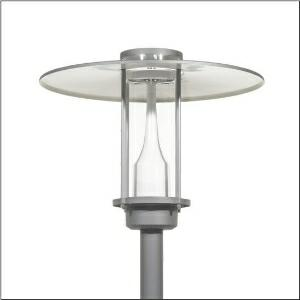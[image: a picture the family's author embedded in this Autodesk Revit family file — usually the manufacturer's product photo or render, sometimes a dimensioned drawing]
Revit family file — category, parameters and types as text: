
# Revit family: city-light_plus_iq___p1_0a_5xa5275ff14hp_3a67
name_source: partatom
category: Lighting Fixtures
units: mm (PartAtom-declared; Revit-internal decimal feet)

## family parameters
Cut with Voids When Loaded = No
Host = Face
Light Source = No
Part Type = Normal
Room Calculation Point = No
Round Connector Dimension = Use Diameter
Shared = No

## types (1)
- --- (1 x LED, 4480 lm, 33.6 W, 3000K)
    Apparent Load = 34 VA
    CIE Flux Codes = 30 60 90 96 100
    Color Rendering = 70
    Color Temperature = 3000K
    Default Elevation = 1800 mm
    Description = City-Light Plus iQ, mast luminaire, Module 540 iQ-SR, primary light control with 3 zone facetted reflector, of plastic, silver coated, highly specular, structured, primary optical cover: cover, of PMMA, transparent, light distribution: P1.0a, light emission: direct distribution, primary light characteristic: strongly asymmetric, installation type: post-top, LED, High Power LED, rated luminous flux: 4.480lm, luminous efficacy: 133lm/W, light colour: 730, colour temperature: 3000K, control gear: iQ Street-Remote, control: pre-setting: logarithmic dimming characteristic, Street-Remote, Auto-Match, Temp-Guard, Lumen-Switch, Night-Set, Smart-Wire, Light-Fading, Desk-Remote (wireless, voltage-free reading and setting of iQ features in the workshop via application-optimized NFC function/RFID function), optimised constant luminous flux control (CLO 2.0), with terminal, 6-pole, max. 2.5mm², mains connection: 230..240V, AC, 50/60Hz, start of lifetime: 34W, end of service life: 36W, reduction: 15W, luminaire housing, upper part, of glass-fibre reinforced polyester, coated, Siteco® metallic grey (DB 702S), diameter: 750mm, height: 590mm, spigot size: d x l = 76 x 70mm (post-top) | with reducer (optional accessory) 60 x 70mm, mounting height: 3..5m, post-top mast mounting element, of diecast aluminium, coated, Siteco® metallic grey (DB 702S), Module 540 iQ-SR, traffic white (RAL 9016), equipment: Power, protection rating (complete): IP65, insulation class (complete): insulation class II (safety insulation), certification: CE, ENEC, VDE, packaging unit: 1 piece

Light Distribution: P1.0a
    Height = 590 mm
    Lamp = 1 x LED
    Lamp Light Flux = 4480 lm
    Lamp Power = 33.6 W
    Lamp count = 1
    Length = 750 mm
    Luminous efficacy = 133 lm/W
    Manufacturer = Siteco
    ModVariant = No
    Model = 5XA5275FF14HP
    Number of Poles = 1
    OnlyDefault = Yes
    Power Factor = 1
    Product Name = City-Light Plus iQ | P1.0a
    Product group = mast luminaire | pylon top
    ProductGroupID = 6100
    Protection Class = Protection class II
    Protection Degree = IP 65
    RLX_Detail_Level = 1
    RLX_Emergency_Light_Flux = 0 lm
    RLX_Emergency_Type = 0
    RLX_Emergency_Type_DB = No
    RlxData = <blob elided: 35113 chars, md5=0dd6beff>
    Socket = socket
    Standby Power = 0 W
    System Light Flux = 4480 lm
    System Power = 34 W
    Type Comments = factory setting: luminous flux: 100 % | dim-lin: 254 | 695 mA
    Type Image = l_1006456.jpg
    URL = http://relux.com
    VarID = @adj_215035
    Voltage = 0 V
    Weight = 0.00 kg
    Width = 0 mm  [stored 0 ft]

note: [stored X ft] marks values corroborated as IEEE doubles in the binary element streams (Revit-internal decimal feet)

## geometry (parser evidence)
native form markers: Blend x4, Sweep x12
no freeform markers — native parametric forms only
